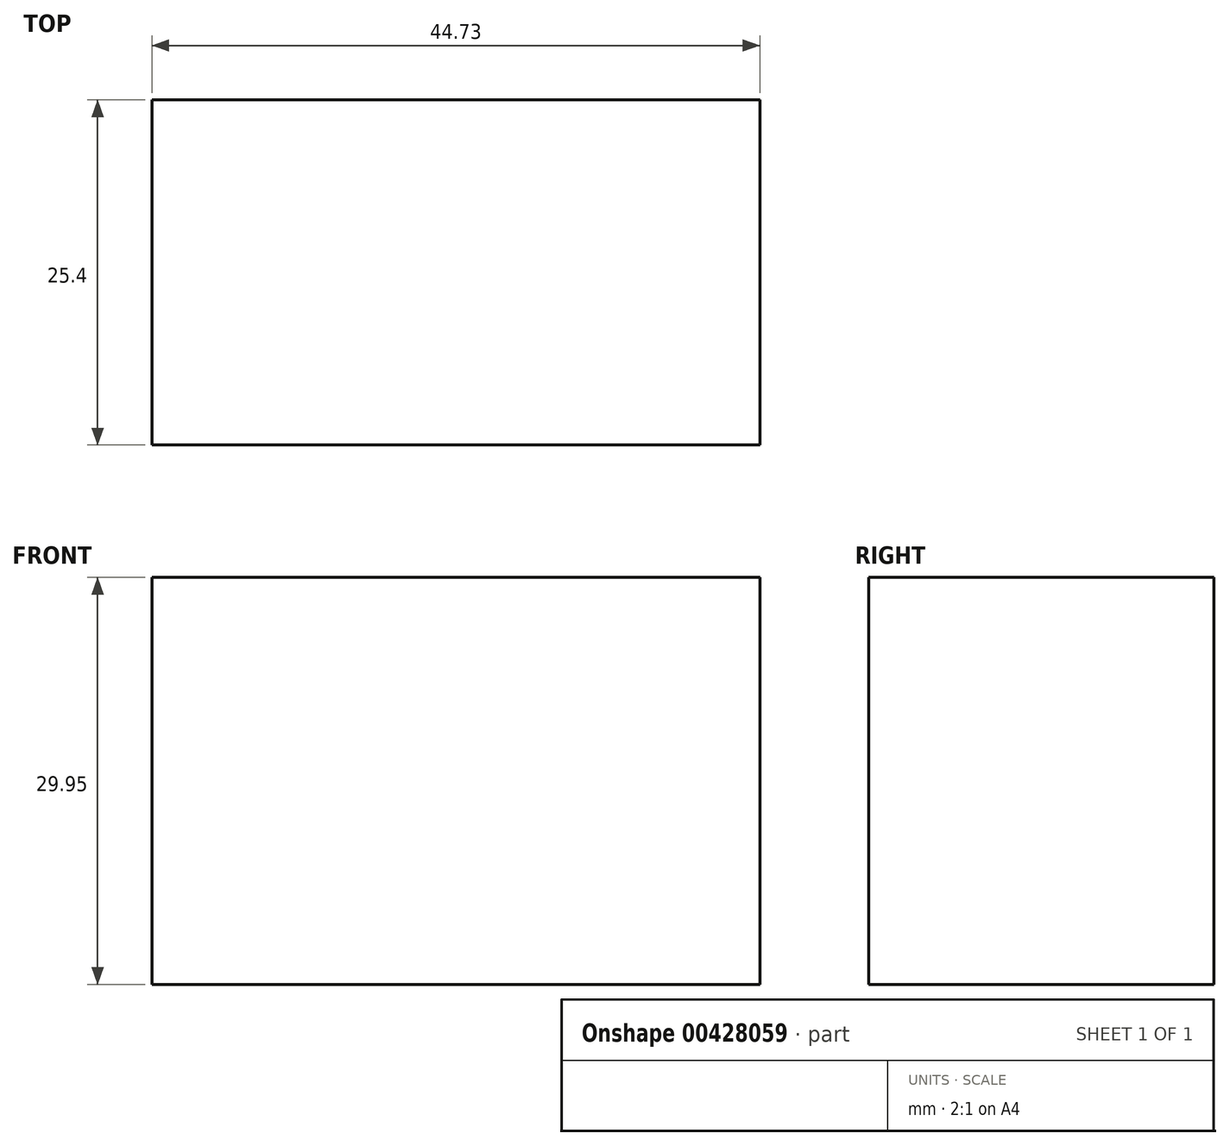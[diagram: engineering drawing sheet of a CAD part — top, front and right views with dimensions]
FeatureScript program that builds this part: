
annotation { "Feature Type Name" : "Feature", "Feature Type Description" : "" }
export const myFeature = defineFeature(function(context is Context, id is Id, definition is map)
    precondition{}
    {
        {
            var Q0;
            Q0=qCreatedBy(makeId("Front.planeOp"),FACE);
            var sketch = newSketch(context, id + "F0", { "sketchPlane" : qUnion([Q0])});
            skLineSegment(sketch, "E0.bottom", {"start": v(0, 0) * mm, "end": v(44.73, 0) * mm});
            skLineSegment(sketch, "E0.top", {"start": v(0, 29.95) * mm, "end": v(44.73, 29.95) * mm});
            skLineSegment(sketch, "E0.left", {"start": v(0, 0) * mm, "end": v(0, 29.95) * mm});
            skLineSegment(sketch, "E0.right", {"start": v(44.73, 0) * mm, "end": v(44.73, 29.95) * mm});
            skSolve(sketch);
        }
        {
            var Q0;
            Q0 = qSketchRegion(id + "F0", true);
            extrude(context, id + "F1", {"entities" : qUnion([Q0]), "depth" : 25.4 * mm, "offsetDistance" : 25.4 * mm});
        }
    });
